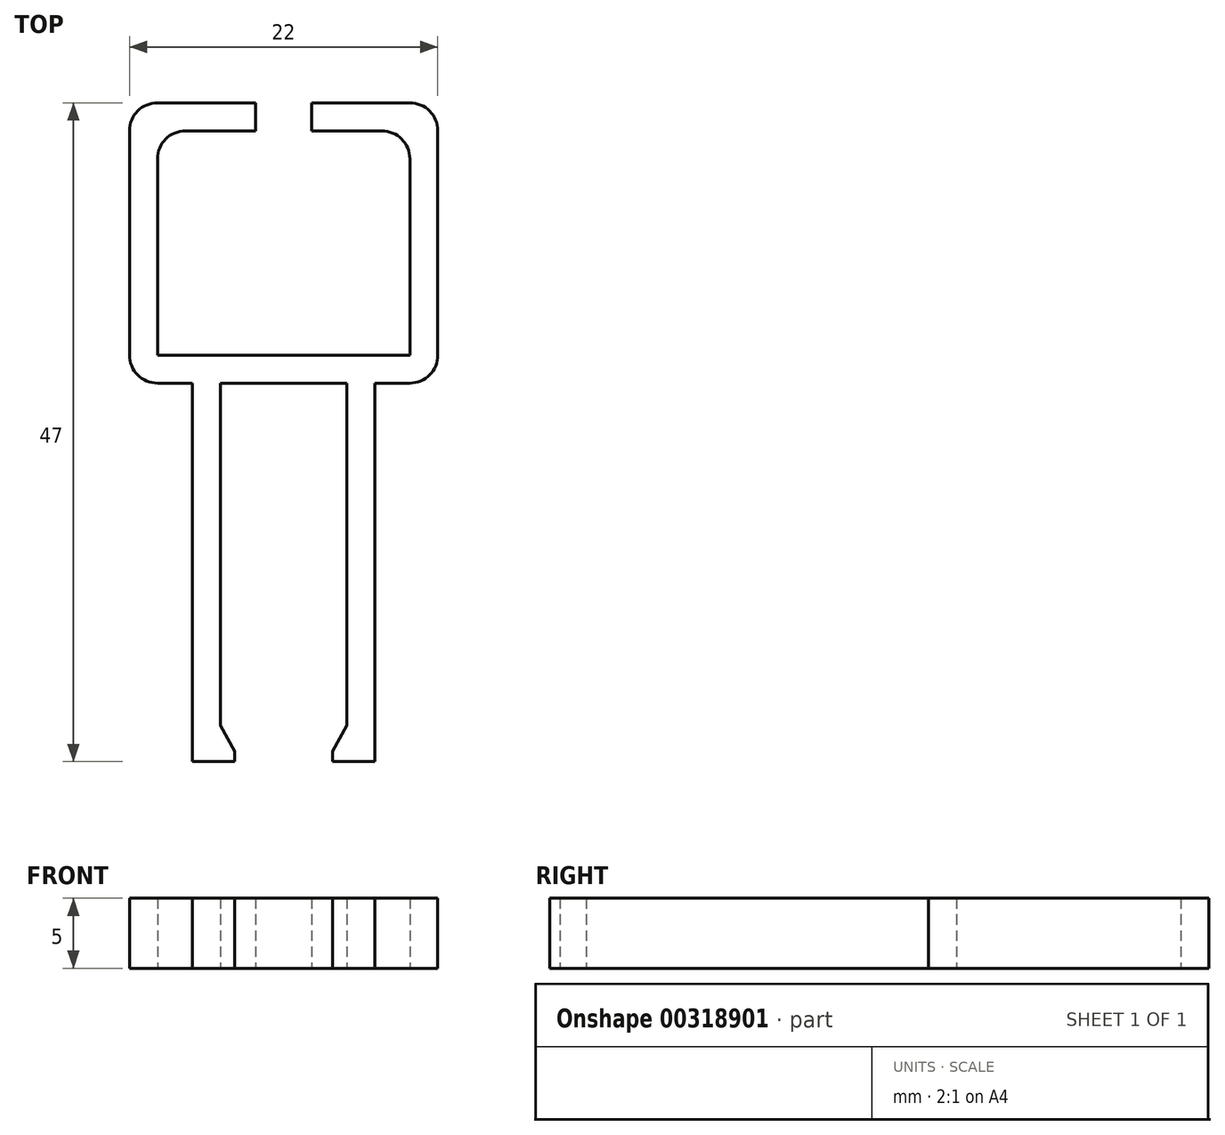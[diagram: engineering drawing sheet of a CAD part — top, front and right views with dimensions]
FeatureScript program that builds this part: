
annotation { "Feature Type Name" : "Feature", "Feature Type Description" : "" }
export const myFeature = defineFeature(function(context is Context, id is Id, definition is map)
    precondition{}
    {
        {
            var Q0;
            Q0=qCreatedBy(makeId("Top.planeOp"),FACE);
            var sketch = newSketch(context, id + "F0", { "sketchPlane" : qUnion([Q0])});
            skLineSegment(sketch, "E0.bottom", {"start": v(0, 12.5) * mm, "end": v(-4.5, 12.5) * mm});
            skLineSegment(sketch, "E0.left", {"start": v(4.5, 12.5) * mm, "end": v(4.5, 0) * mm});
            skPoint(sketch, "E0.middle", {"position": v(0, 0) * mm});
            skLineSegment(sketch, "E1", {"start": v(0, 12.5) * mm, "end": v(4.5, 12.5) * mm});
            skPoint(sketch, "E0.top.end.orphan", {"position": v(-4.5, -12.5) * mm});
            skPoint(sketch, "E0.top.start.orphan", {"position": v(4.5, -12.5) * mm});
            skLineSegment(sketch, "E2", {"start": v(-9, 14.5) * mm, "end": v(-9, 28.5) * mm});
            skLineSegment(sketch, "E3", {"start": v(-7, 30.5) * mm, "end": v(-2, 30.5) * mm});
            skLineSegment(sketch, "E4", {"start": v(9, 14.5) * mm, "end": v(9, 28.5) * mm});
            skLineSegment(sketch, "E5.bottom", {"start": v(9, 32.5) * mm, "end": v(2, 32.5) * mm});
            skLineSegment(sketch, "E5.top", {"start": v(9, 12.5) * mm, "end": v(6.5, 12.5) * mm});
            skLineSegment(sketch, "E5.left", {"start": v(11, 30.5) * mm, "end": v(11, 14.5) * mm});
            skLineSegment(sketch, "E5.right", {"start": v(-11, 30.5) * mm, "end": v(-11, 14.5) * mm});
            skPoint(sketch, "E5.middle", {"position": v(0, 22.5) * mm});
            skLineSegment(sketch, "E6.trimOffspring", {"start": v(-6.5, 12.5) * mm, "end": v(-9, 12.5) * mm});
            skLineSegment(sketch, "E7.trimOffspring", {"start": v(4.5, 12.5) * mm, "end": v(-4.5, 12.5) * mm});
            skLineSegment(sketch, "E8", {"start": v(-9, 14.5) * mm, "end": v(9, 14.5) * mm});
            skArc(sketch, "E9", {"start": v(-11, 14.5) * mm, "mid": v(-10.41, 13.09) * mm, "end": v(-9, 12.5) * mm});
            skArc(sketch, "E10", {"start": v(-9, 32.5) * mm, "mid": v(-10.41, 31.91) * mm, "end": v(-11, 30.5) * mm});
            skArc(sketch, "E11", {"start": v(11, 30.5) * mm, "mid": v(10.41, 31.91) * mm, "end": v(9, 32.5) * mm});
            skPoint(sketch, "E12.orphan", {"position": v(-11, 12.5) * mm});
            skPoint(sketch, "E13.orphan", {"position": v(-11, 32.5) * mm});
            skPoint(sketch, "E14.orphan", {"position": v(11, 32.5) * mm});
            skPoint(sketch, "E15.orphan", {"position": v(11, 12.5) * mm});
            skArc(sketch, "E16.trimOffspring", {"start": v(9, 12.5) * mm, "mid": v(10.41, 13.09) * mm, "end": v(11, 14.5) * mm});
            skPoint(sketch, "E17", {"position": v(2, 30.5) * mm});
            skPoint(sketch, "E18", {"position": v(0, 30.5) * mm});
            skPoint(sketch, "E19", {"position": v(-2, 30.5) * mm});
            skLineSegment(sketch, "E20", {"start": v(-2, 30.5) * mm, "end": v(-2, 32.5) * mm});
            skLineSegment(sketch, "E21", {"start": v(2, 30.5) * mm, "end": v(2, 32.5) * mm});
            skLineSegment(sketch, "E22.trimOffspring", {"start": v(2, 30.5) * mm, "end": v(7, 30.5) * mm});
            skLineSegment(sketch, "E23.trimOffspring", {"start": v(-2, 32.5) * mm, "end": v(-9, 32.5) * mm});
            skPoint(sketch, "E24", {"position": v(-7, 28.5) * mm});
            skPoint(sketch, "E25", {"position": v(7, 28.5) * mm});
            skArc(sketch, "E26", {"start": v(-7, 30.5) * mm, "mid": v(-8.41, 29.91) * mm, "end": v(-9, 28.5) * mm});
            skArc(sketch, "E27", {"start": v(9, 28.5) * mm, "mid": v(8.41, 29.91) * mm, "end": v(7, 30.5) * mm});
            skLineSegment(sketch, "E28.left", {"start": v(4.5, 0) * mm, "end": v(4.5, -11.92) * mm});
            skLineSegment(sketch, "E29.top", {"start": v(6.5, -14.5) * mm, "end": v(3.5, -14.5) * mm});
            skLineSegment(sketch, "E29.left", {"start": v(6.5, -12.5) * mm, "end": v(6.5, -14.5) * mm});
            skLineSegment(sketch, "E29.right", {"start": v(3.5, -13.78) * mm, "end": v(3.5, -14.5) * mm});
            skPoint(sketch, "E30.right.start.orphan", {"position": v(6.5, 1) * mm});
            skLineSegment(sketch, "E31", {"start": v(6.5, 12.5) * mm, "end": v(6.5, -12.5) * mm});
            skLineSegment(sketch, "E32", {"start": v(-6.5, 12.5) * mm, "end": v(-6.5, -12.5) * mm});
            skLineSegment(sketch, "E33.top", {"start": v(-6.5, -14.5) * mm, "end": v(-3.5, -14.5) * mm});
            skLineSegment(sketch, "E33.left", {"start": v(-6.5, -12.5) * mm, "end": v(-6.5, -14.5) * mm});
            skLineSegment(sketch, "E33.right", {"start": v(-3.5, -13.78) * mm, "end": v(-3.5, -14.5) * mm});
            skLineSegment(sketch, "E34", {"start": v(-4.5, -11.92) * mm, "end": v(-4.5, 12.5) * mm});
            skLineSegment(sketch, "E35", {"start": v(-3.5, -13.78) * mm, "end": v(-4.5, -11.92) * mm});
            skLineSegment(sketch, "E36", {"start": v(3.5, -13.78) * mm, "end": v(4.5, -11.92) * mm});
            skSolve(sketch);
        }
        {
            var Q0;
            Q0=makeQuery(id+"F0.imprint","IMPRINT",FACE,{"disambiguationData":[TD([[makeQuery(id+"F0.imprint","IMPRINT",EDGE,{"derivedFrom":sQuery(id+"F0.wireOp",EDGE,"E0.left")}),1.0]])]});
            extrude(context, id + "F1", {"entities" : qUnion([Q0]), "depth" : 5 * mm});
        }
    });
